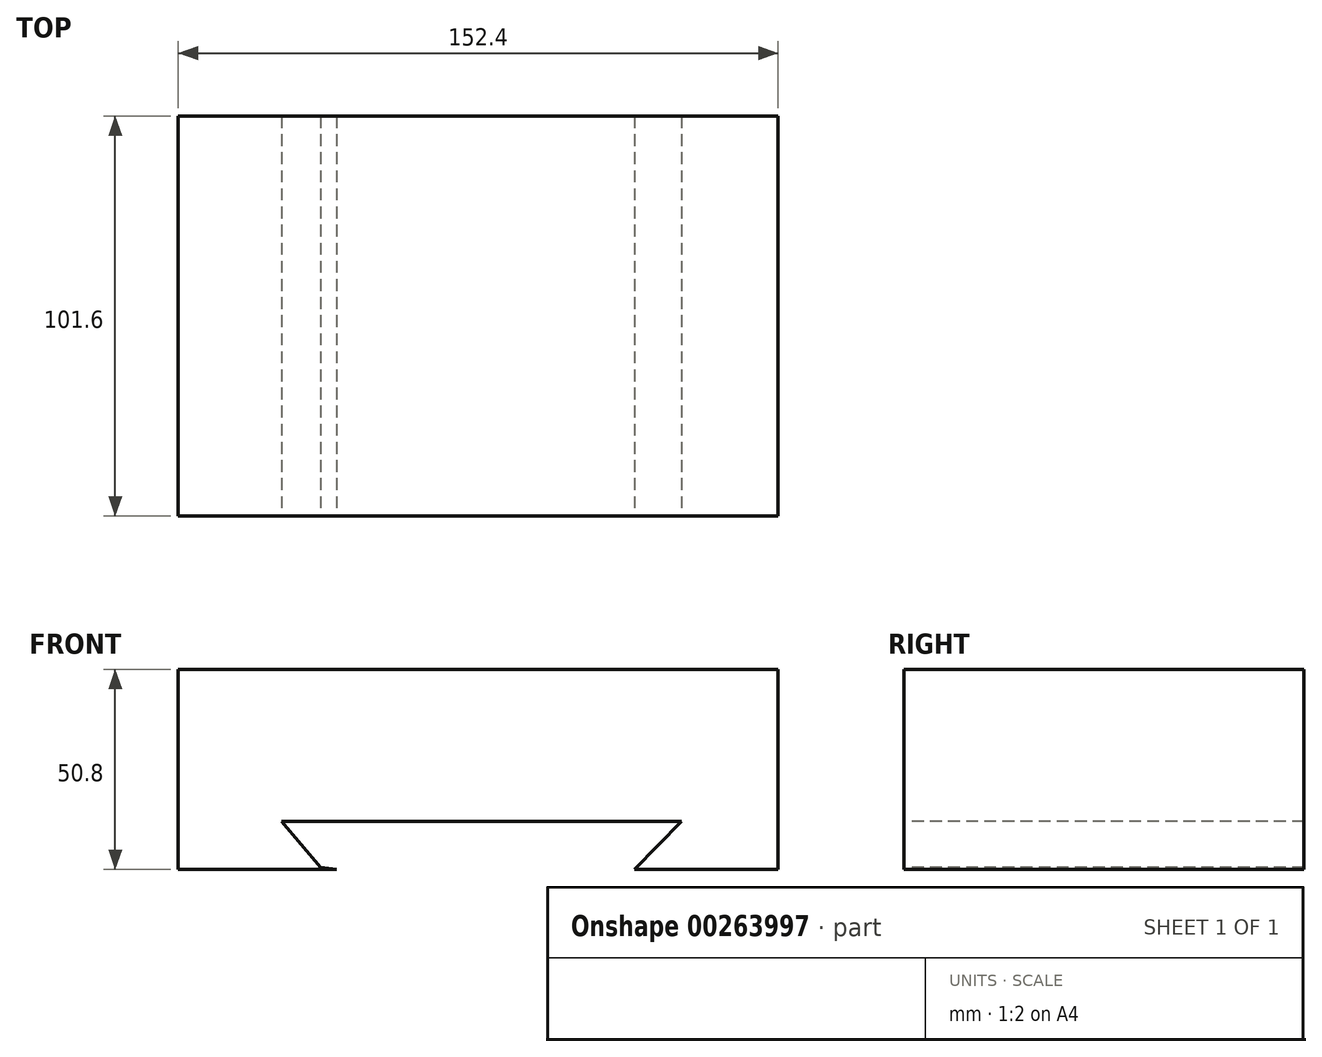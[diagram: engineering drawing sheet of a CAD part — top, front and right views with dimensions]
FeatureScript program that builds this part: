
annotation { "Feature Type Name" : "Feature", "Feature Type Description" : "" }
export const myFeature = defineFeature(function(context is Context, id is Id, definition is map)
    precondition{}
    {
        {
            var Q0;
            Q0=qCreatedBy(makeId("Front.planeOp"),FACE);
            var sketch = newSketch(context, id + "F0", { "sketchPlane" : qUnion([Q0])});
            skLineSegment(sketch, "E0.bottom", {"start": v(-75.09, -25.74) * mm, "end": v(77.31, -25.74) * mm});
            skLineSegment(sketch, "E0.top", {"start": v(-75.09, -76.54) * mm, "end": v(77.31, -76.54) * mm});
            skLineSegment(sketch, "E0.left", {"start": v(-75.09, -25.74) * mm, "end": v(-75.09, -76.54) * mm});
            skLineSegment(sketch, "E0.right", {"start": v(77.31, -25.74) * mm, "end": v(77.31, -76.54) * mm});
            skSolve(sketch);
        }
        {
            var Q0;
            Q0=makeQuery(id+"F0.imprint","IMPRINT",FACE,{"disambiguationData":[TD([[makeQuery(id+"F0.imprint","IMPRINT",EDGE,{"derivedFrom":sQuery(id+"F0.wireOp",EDGE,"E0.bottom")}),-1.0]])]});
            extrude(context, id + "F1", {"entities" : qUnion([Q0]), "depth" : 25.4 * mm});
        }
        {
            var Q0;
            Q0=makeQuery(id+"F1.opExtrude","CAP_FACE",FACE,{"disambiguationData":[OSD([sQuery(id+"F0.wireOp",EDGE,"E0.bottom"),sQuery(id+"F0.wireOp",EDGE,"E0.top"),sQuery(id+"F0.wireOp",EDGE,"E0.left"),sQuery(id+"F0.wireOp",EDGE,"E0.right")])],"isStart":false});
            var sketch = newSketch(context, id + "F2", { "sketchPlane" : qUnion([Q0])});
            skLineSegment(sketch, "E1", {"start": v(-75.09, -76.54) * mm, "end": v(-36.99, -76.54) * mm, "construction": true});
            skLineSegment(sketch, "E2", {"start": v(-75.09, -63.84) * mm, "end": v(-49.69, -63.84) * mm, "construction": true});
            skLineSegment(sketch, "E3", {"start": v(-49.69, -76.54) * mm, "end": v(-49.69, -63.84) * mm, "construction": true});
            skSolve(sketch);
        }
        {
            var Q0;
            Q0=makeQuery(id+"F2.imprint","IMPRINT",FACE,{"disambiguationData":[TD([[makeQuery(id+"F2.imprint","IMPRINT",EDGE,{"derivedFrom":makeQuery(id+"F1.opExtrude","CAP_EDGE",EDGE,{"disambiguationData":[OSD([sQuery(id+"F0.wireOp",EDGE,"E0.bottom")])],"isStart":false})}),-1.0]])]});
            var sketch = newSketch(context, id + "F3", { "sketchPlane" : qUnion([Q0])});
            skLineSegment(sketch, "E4", {"start": v(-48.83, -64.38) * mm, "end": v(52.77, -64.38) * mm});
            skLineSegment(sketch, "E5", {"start": v(-48.83, -64.38) * mm, "end": v(-38.93, -75.97) * mm});
            skLineSegment(sketch, "E6", {"start": v(41.64, -75.72) * mm, "end": v(52.77, -64.38) * mm});
            skLineSegment(sketch, "E7", {"start": v(-38.93, -75.97) * mm, "end": v(-3.4, -80.95) * mm});
            skLineSegment(sketch, "E8", {"start": v(41.64, -75.72) * mm, "end": v(37.37, -80.06) * mm});
            skLineSegment(sketch, "E9", {"start": v(37.37, -80.06) * mm, "end": v(-3.4, -80.95) * mm});
            skSolve(sketch);
        }
        {
            var Q0;
            Q0 = qSketchRegion(id + "F3", true);
            extrude(context, id + "F4", {"entities" : qUnion([Q0]), "operationType" : NewBodyOperationType.REMOVE, "oppositeDirection" : true, "depth" : 25.4 * mm});
        }
        {
            var Q0;
            Q0=makeQuery(id+"F1.opExtrude","CAP_FACE",FACE,{"disambiguationData":[OSD([sQuery(id+"F0.wireOp",EDGE,"E0.bottom"),sQuery(id+"F0.wireOp",EDGE,"E0.top"),sQuery(id+"F0.wireOp",EDGE,"E0.left"),sQuery(id+"F0.wireOp",EDGE,"E0.right")])],"isStart":true});
            extrude(context, id + "F5", {"entities" : qUnion([Q0]), "operationType" : NewBodyOperationType.ADD, "depth" : 76.2 * mm});
        }
    });
